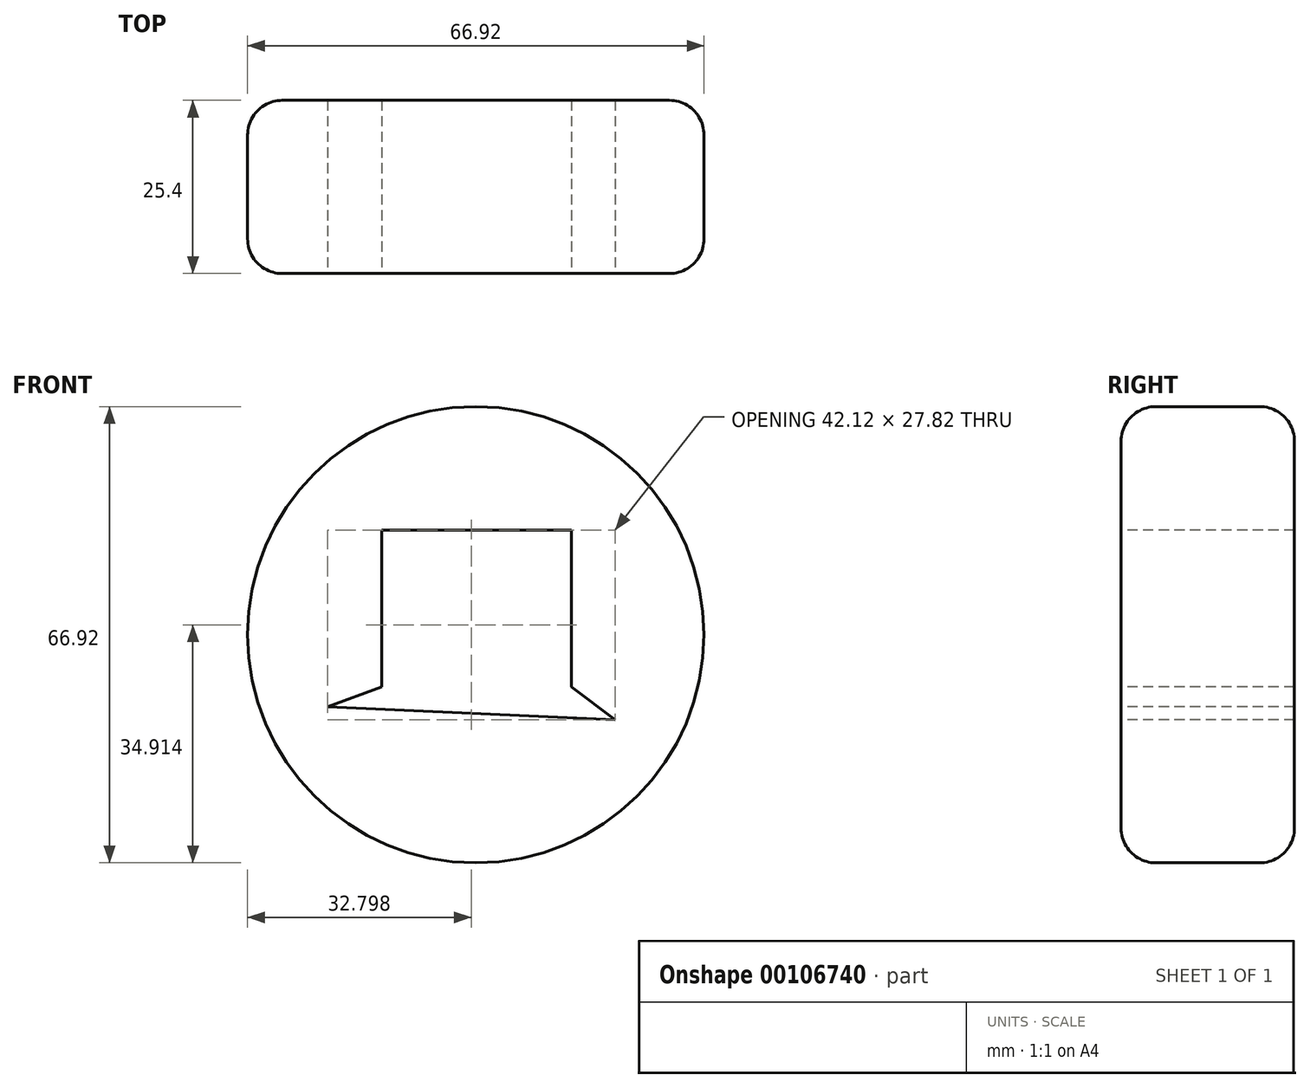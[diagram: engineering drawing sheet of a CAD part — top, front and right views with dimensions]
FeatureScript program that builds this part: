
annotation { "Feature Type Name" : "Feature", "Feature Type Description" : "" }
export const myFeature = defineFeature(function(context is Context, id is Id, definition is map)
    precondition{}
    {
        {
            var Q0;
            Q0=qCreatedBy(makeId("Front.planeOp"),FACE);
            var sketch = newSketch(context, id + "F0", { "sketchPlane" : qUnion([Q0])});
            skCircle(sketch, "E0", {"center": v(0, 0) * mm, "radius": 33.46 * mm});
            skSolve(sketch);
        }
        {
            var Q0;
            Q0 = qSketchRegion(id + "F0", true);
            extrude(context, id + "F1", {"entities" : qUnion([Q0]), "depth" : 25.4 * mm});
        }
        {
            var Q0;
            Q0=makeQuery(id+"F1.opExtrude","CAP_EDGE",EDGE,{"disambiguationData":[OSD([sQuery(id+"F0.wireOp",EDGE,"E0")])],"isStart":false});
            fillet(context, id + "F2", {"entities" : qUnion([Q0]), "radius" : 5.08 * mm, "tangentPropagation" : true, "allowEdgeOverflow" : false});
        }
        {
            var Q0;
            Q0=makeQuery(id+"F1.opExtrude","CAP_EDGE",EDGE,{"disambiguationData":[OSD([sQuery(id+"F0.wireOp",EDGE,"E0")])],"isStart":true});
            fillet(context, id + "F3", {"entities" : qUnion([Q0]), "radius" : 5.08 * mm, "tangentPropagation" : true, "allowEdgeOverflow" : false});
        }
        {
            var Q0;
            Q0=makeQuery(id+"F1.opExtrude","CAP_FACE",FACE,{"disambiguationData":[OSD([sQuery(id+"F0.wireOp",EDGE,"E0")])],"isStart":false});
            var sketch = newSketch(context, id + "F4", { "sketchPlane" : qUnion([Q0])});
            skLineSegment(sketch, "E1", {"start": v(-13.78, 15.36) * mm, "end": v(14.04, 15.36) * mm});
            skLineSegment(sketch, "E2", {"start": v(14.04, 15.36) * mm, "end": v(14.04, -7.69) * mm});
            skLineSegment(sketch, "E3", {"start": v(14.04, -7.69) * mm, "end": v(-13.78, -7.69) * mm});
            skLineSegment(sketch, "E4", {"start": v(-13.78, -7.69) * mm, "end": v(-13.78, 15.36) * mm});
            skSolve(sketch);
        }
        {
            var Q0;
            Q0 = qSketchRegion(id + "F4", true);
            extrude(context, id + "F5", {"entities" : qUnion([Q0]), "operationType" : NewBodyOperationType.REMOVE, "endBound" : BoundingType.THROUGH_ALL, "oppositeDirection" : true, "depth" : 25.4 * mm});
        }
        {
            var Q0;
            Q0=makeQuery(id+"F1.opExtrude","CAP_FACE",FACE,{"disambiguationData":[OSD([sQuery(id+"F0.wireOp",EDGE,"E0")])],"isStart":false});
            var sketch = newSketch(context, id + "F6", { "sketchPlane" : qUnion([Q0])});
            skLineSegment(sketch, "E5", {"start": v(-21.72, -10.6) * mm, "end": v(-13.78, -7.69) * mm});
            skLineSegment(sketch, "E6", {"start": v(-13.78, -7.69) * mm, "end": v(14.04, -7.69) * mm});
            skLineSegment(sketch, "E7", {"start": v(14.04, -7.69) * mm, "end": v(20.4, -12.45) * mm});
            skLineSegment(sketch, "E8", {"start": v(20.4, -12.45) * mm, "end": v(-21.72, -10.6) * mm});
            skSolve(sketch);
        }
        {
            var Q0;
            Q0 = qSketchRegion(id + "F6", true);
            extrude(context, id + "F7", {"entities" : qUnion([Q0]), "operationType" : NewBodyOperationType.REMOVE, "endBound" : BoundingType.THROUGH_ALL, "oppositeDirection" : true, "depth" : 25.4 * mm});
        }
    });
